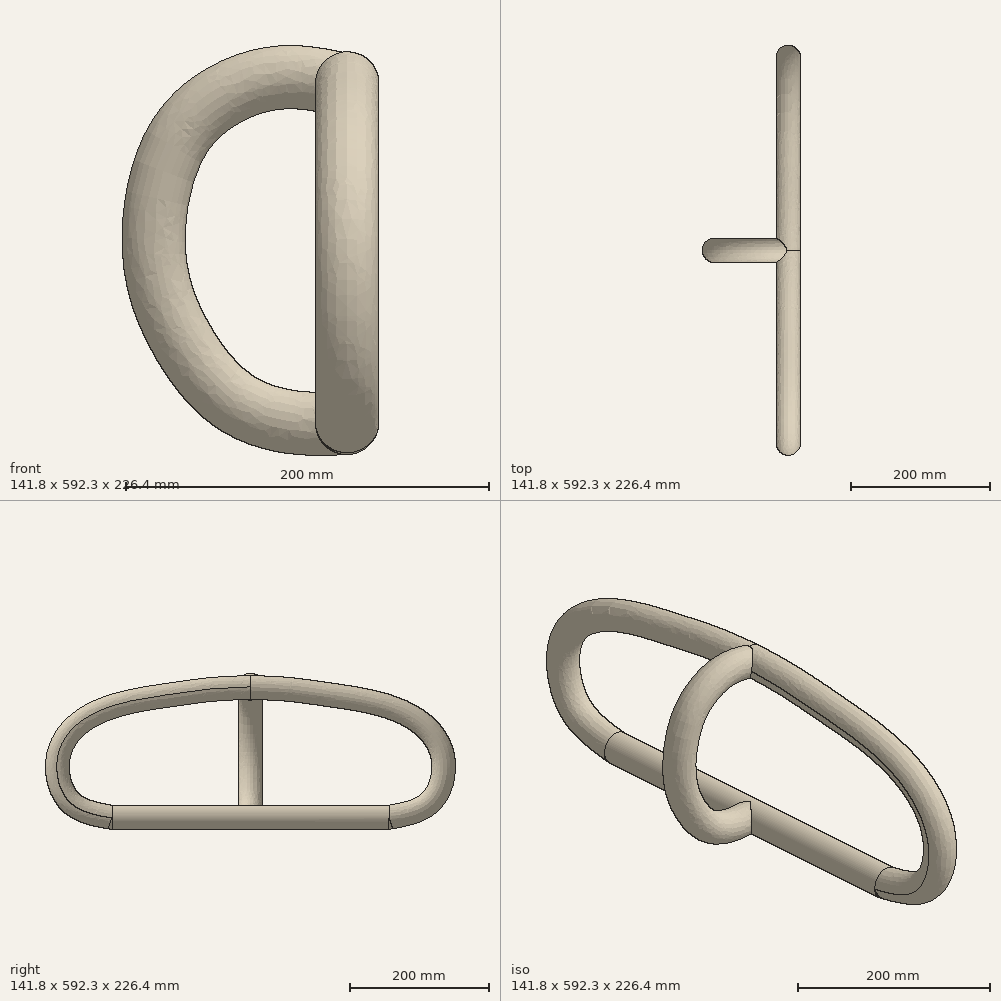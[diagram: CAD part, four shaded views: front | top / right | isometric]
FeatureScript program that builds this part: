
annotation { "Feature Type Name" : "Feature", "Feature Type Description" : "" }
export const myFeature = defineFeature(function(context is Context, id is Id, definition is map)
    precondition{}
    {
        {
            var Q0;
            Q0=qCreatedBy(makeId("Front.planeOp"),FACE);
            var sketch = newSketch(context, id + "F0", { "sketchPlane" : qUnion([Q0])});
            skCircle(sketch, "E0", {"center": v(0, 0) * mm, "radius": 17.5 * mm});
            skSolve(sketch);
        }
        {
            var Q0;
            Q0=makeQuery(id+"F0.imprint","IMPRINT",FACE,{"disambiguationData":[TD([[makeQuery(id+"F0.imprint","IMPRINT",EDGE,{"derivedFrom":sQuery(id+"F0.wireOp",EDGE,"E0")}),1.0]])]});
            extrude(context, id + "F1", {"entities" : qUnion([Q0]), "depth" : 200 * mm, "offsetDistance" : 25 * mm, "hasSecondDirection" : true, "secondDirectionOppositeDirection" : true, "secondDirectionDepth" : 200 * mm});
        }
        {
            var Q0;
            Q0=qCreatedBy(makeId("Right.planeOp"),FACE);
            var sketch = newSketch(context, id + "F2", { "sketchPlane" : qUnion([Q0])});
            skFitSpline(sketch, "E1", {"points": [v(-199.65, 0) * mm, v(-261.96, 24.32) * mm, v(-276, 93.65) * mm, v(-220.72, 151.57) * mm, v(-119.8, 176.14) * mm, v(-53.1, 184.92) * mm, v(0, 187.55) * mm], "startDerivative": vector(-446.87, 78.19) * mm, "endDerivative": vector(369.34, 10.7) * mm});
            skFitSpline(sketch, "E2.MirrorCS", {"points": [v(199.65, 0) * mm, v(261.96, 24.32) * mm, v(276, 93.65) * mm, v(220.72, 151.57) * mm, v(119.8, 176.14) * mm, v(53.1, 184.92) * mm, v(0, 187.55) * mm], "startDerivative": vector(446.87, 78.19) * mm, "endDerivative": vector(-369.34, 10.7) * mm});
            skSolve(sketch);
        }
        {
            var Q0;
            Q0=makeQuery(id+"F1.opExtrude","CAP_FACE",FACE,{"disambiguationData":[OSD([sQuery(id+"F0.wireOp",EDGE,"E0")])],"isStart":false});
            var Q1;
            Q1=sQuery(id+"F2.wireOp",EDGE,"E1");
            var Q2;
            Q2=sQuery(id+"F2.wireOp",EDGE,"E2.MirrorCS");
            sweep(context, id + "F3", {"operationType" : NewBodyOperationType.ADD, "profiles" : qUnion([Q0]), "path" : qUnion([Q1, Q2])});
        }
        {
            var Q0;
            {var subQ0=sQuery(id+"F0.wireOp",EDGE,"E0");Q0=makeQuery(id+"F3.boolean.opBoolean","SPLIT",FACE,{"disambiguationData":[TD([makeQuery(id+"F1.opExtrude","SWEPT_FACE",FACE,{"disambiguationData":[OSD([subQ0])]}),makeQuery(id+"F3.opSweep","SWEPT_FACE",FACE,{"disambiguationData":[OSD([subQ0,sQuery(id+"F2.wireOp",EDGE,"E2.MirrorCS")])]}),makeQuery(id+"F3.opSweep","CAP_FACE",FACE,{"disambiguationData":[OSD([subQ0,sQuery(id+"F2.wireOp",VERTEX,"E2.MirrorCS.start")])],"isStart":false})])],"derivedFrom":makeQuery(id+"F1.opExtrude","CAP_FACE",FACE,{"disambiguationData":[OSD([subQ0])],"isStart":true})});}
            var Q1;
            Q1 = qConstructionFilter(qBodyType(qCreatedBy(id + "F2" ,EDGE), BodyType.WIRE), ConstructionObject.NO);
            sweep(context, id + "F4", {"operationType" : NewBodyOperationType.ADD, "profiles" : qUnion([Q0]), "path" : qUnion([Q1])});
        }
        {
            var Q0;
            Q0=qCreatedBy(makeId("Front.planeOp"),FACE);
            var sketch = newSketch(context, id + "F5", { "sketchPlane" : qUnion([Q0])});
            skFitSpline(sketch, "E3.MirrorCS", {"points": [v(0, 0) * mm, v(-27.12, 0) * mm, v(-62.57, 12.04) * mm, v(-92.63, 48.26) * mm, v(-106.5, 92.96) * mm, v(-95.71, 152.3) * mm, v(-66.43, 181.6) * mm, v(-33.29, 190.84) * mm, v(0, 186.22) * mm], "startDerivative": vector(-254.62, -14.83) * mm, "endDerivative": vector(291.66, -65.3) * mm});
            skSolve(sketch);
        }
        {
            var Q0;
            Q0=qCreatedBy(makeId("Right.planeOp"),FACE);
            var sketch = newSketch(context, id + "F6", { "sketchPlane" : qUnion([Q0])});
            skCircle(sketch, "E4", {"center": v(0, 0) * mm, "radius": 17.5 * mm});
            skSolve(sketch);
        }
        {
            var Q0;
            Q0 = qSketchRegion(id + "F6", true);
            var Q1;
            Q1=sQuery(id+"F5.wireOp",EDGE,"E3.MirrorCS");
            sweep(context, id + "F7", {"operationType" : NewBodyOperationType.ADD, "profiles" : qUnion([Q0]), "path" : qUnion([Q1])});
        }
    });
